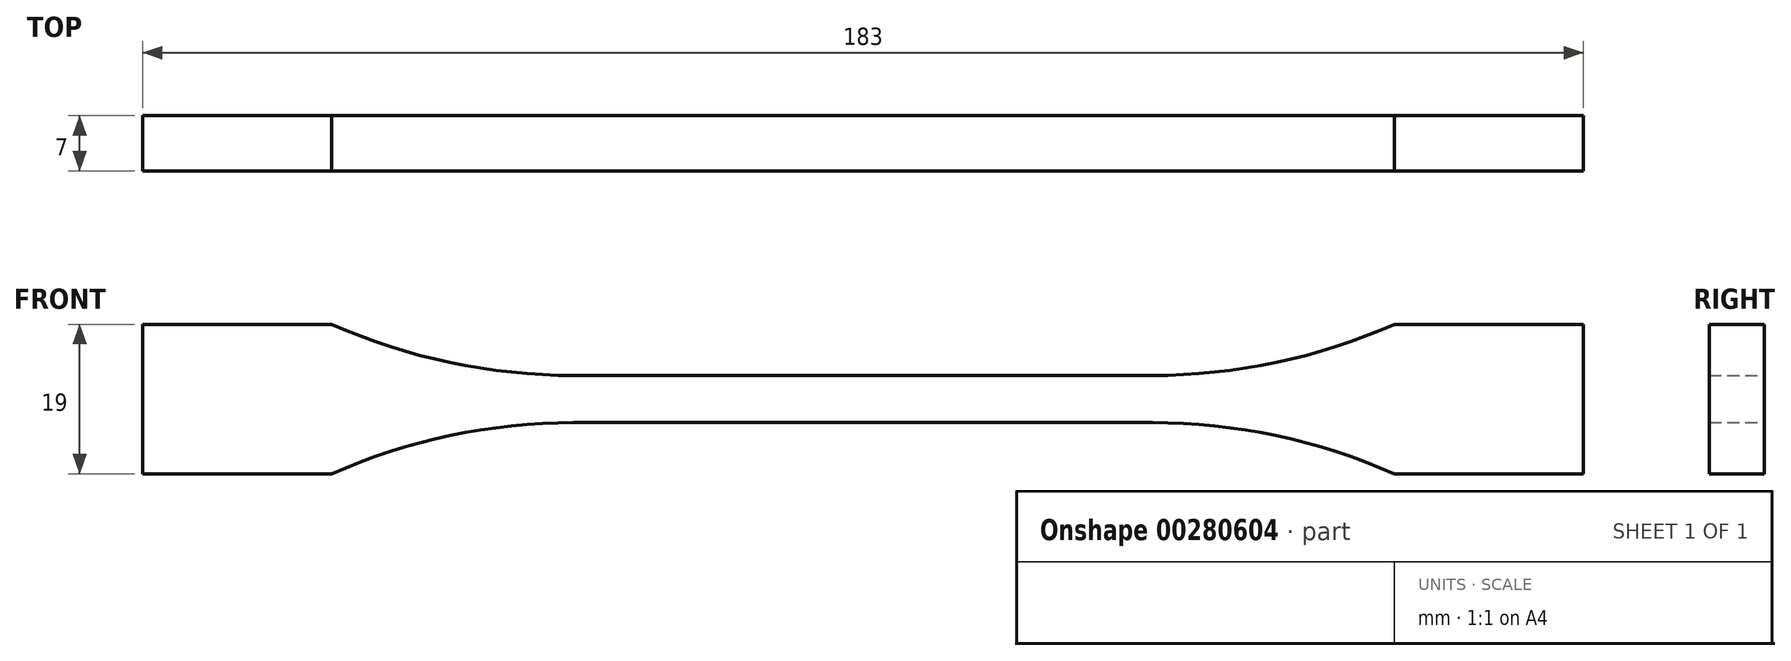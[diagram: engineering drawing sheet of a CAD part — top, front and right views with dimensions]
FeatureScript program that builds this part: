
annotation { "Feature Type Name" : "Feature", "Feature Type Description" : "" }
export const myFeature = defineFeature(function(context is Context, id is Id, definition is map)
    precondition{}
    {
        {
            var Q0;
            Q0=qCreatedBy(makeId("Front.planeOp"),FACE);
            var sketch = newSketch(context, id + "F0", { "sketchPlane" : qUnion([Q0])});
            skLineSegment(sketch, "E0", {"start": v(0, 3) * mm, "end": v(36.75, 3) * mm});
            skArc(sketch, "E1", {"start": v(36.75, 3) * mm, "mid": v(52.46, 4.64) * mm, "end": v(67.5, 9.5) * mm});
            skLineSegment(sketch, "E2", {"start": v(67.5, 9.5) * mm, "end": v(91.5, 9.5) * mm});
            skLineSegment(sketch, "E3.MirrorCS", {"start": v(67.5, -9.5) * mm, "end": v(91.5, -9.5) * mm});
            skLineSegment(sketch, "E4.MirrorCS", {"start": v(0, -3) * mm, "end": v(36.75, -3) * mm});
            skArc(sketch, "E5.MirrorCS", {"start": v(36.75, -3) * mm, "mid": v(52.46, -4.64) * mm, "end": v(67.5, -9.5) * mm});
            skLineSegment(sketch, "E6.MirrorCS", {"start": v(0, -3) * mm, "end": v(-36.75, -3) * mm});
            skArc(sketch, "E7.MirrorCS", {"start": v(-36.75, 3) * mm, "mid": v(-52.46, 4.64) * mm, "end": v(-67.5, 9.5) * mm});
            skLineSegment(sketch, "E8.MirrorCS", {"start": v(-67.5, 9.5) * mm, "end": v(-91.5, 9.5) * mm});
            skLineSegment(sketch, "E9.MirrorCS", {"start": v(-67.5, -9.5) * mm, "end": v(-91.5, -9.5) * mm});
            skLineSegment(sketch, "E10.MirrorCS", {"start": v(0, 3) * mm, "end": v(-36.75, 3) * mm});
            skArc(sketch, "E11.MirrorCS", {"start": v(-36.75, -3) * mm, "mid": v(-52.46, -4.64) * mm, "end": v(-67.5, -9.5) * mm});
            skLineSegment(sketch, "E12", {"start": v(-91.5, -9.5) * mm, "end": v(-91.5, 9.5) * mm});
            skLineSegment(sketch, "E13", {"start": v(91.5, -9.5) * mm, "end": v(91.5, 9.5) * mm});
            skSolve(sketch);
        }
        {
            var Q0;
            Q0=makeQuery(id+"F0.imprint","IMPRINT",FACE,{"disambiguationData":[TD([[makeQuery(id+"F0.imprint","IMPRINT",EDGE,{"derivedFrom":sQuery(id+"F0.wireOp",EDGE,"E4.MirrorCS")}),1.0]])]});
            extrude(context, id + "F1", {"entities" : qUnion([Q0]), "endBound" : BoundingType.SYMMETRIC, "depth" : 7 * mm});
        }
    });
